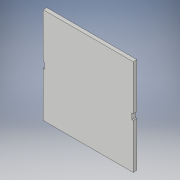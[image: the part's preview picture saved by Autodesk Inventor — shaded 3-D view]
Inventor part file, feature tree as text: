
AUTODESK INVENTOR PART (.ipt)
format: ipt  version: 2018 (Build 220112000, 112)  size: 101,376 bytes
history: native  units: in
note: dims shown in document units (in); Inventor stores cm internally (conversion verified against a paired STEP export)
features: extrude x1, sketch x1
ambient origin geometry x8: Origin, YZ Plane, XZ Plane, XY Plane, X Axis, Y Axis, Z Axis, Center Point
bodies: Solid1 (feature_tree)
feature tree (2):
  extrude  "Extrusion1"  Depth=26.086in
  sketch  "Sketch1"  dims[d0=24.522in d1=26.086in d2=0.7875in d3=1.575in d4=0.369in d5=1.0in d6=0.0in]
